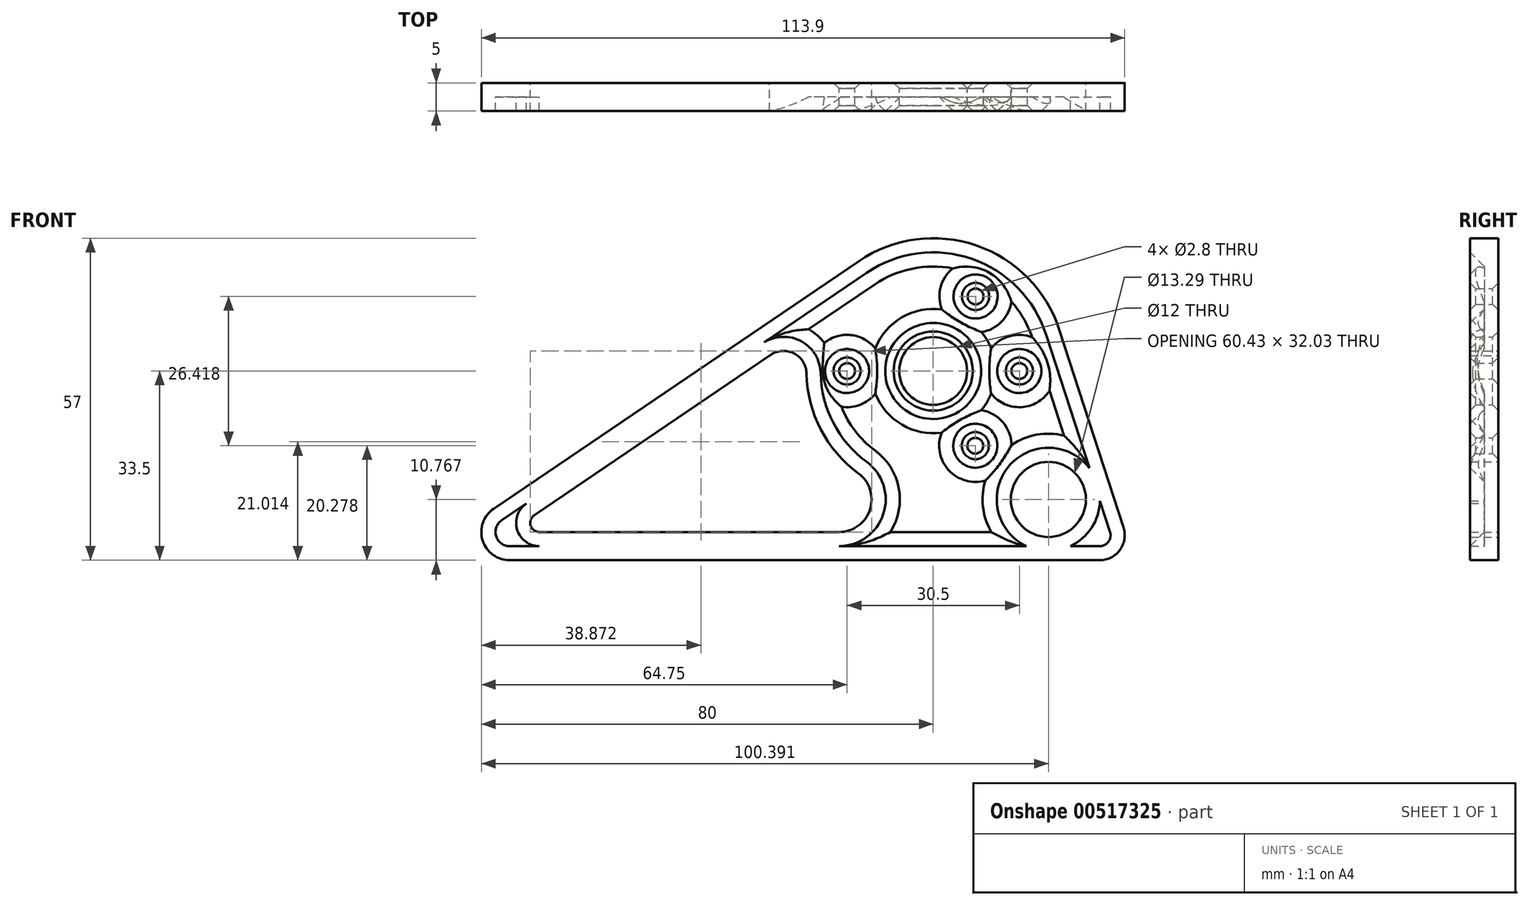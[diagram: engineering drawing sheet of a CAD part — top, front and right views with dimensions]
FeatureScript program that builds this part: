
annotation { "Feature Type Name" : "Feature", "Feature Type Description" : "" }
export const myFeature = defineFeature(function(context is Context, id is Id, definition is map)
    precondition{}
    {
        {
            var Q0;
            Q0=qCreatedBy(makeId("Front.planeOp"),FACE);
            var sketch = newSketch(context, id + "F0", { "sketchPlane" : qUnion([Q0])});
            skCircle(sketch, "E0", {"center": v(0, 0) * mm, "radius": 18.5 * mm});
            skCircle(sketch, "E1", {"center": v(0, 0) * mm, "radius": 6 * mm});
            skArc(sketch, "E2", {"start": v(-1.66, 2.5) * mm, "mid": v(0, -3) * mm, "end": v(1.66, 2.5) * mm});
            skLineSegment(sketch, "E3", {"start": v(-1.66, 2.5) * mm, "end": v(1.66, 2.5) * mm});
            skCircle(sketch, "E4", {"center": v(-15.25, 0) * mm, "radius": 1.4 * mm});
            skCircle(sketch, "E5", {"center": v(15.25, 0) * mm, "radius": 1.4 * mm});
            skCircle(sketch, "E6", {"center": v(7.5, 13.2) * mm, "radius": 1.4 * mm});
            skCircle(sketch, "E7", {"center": v(7.45, -13.22) * mm, "radius": 1.4 * mm});
            skLineSegment(sketch, "E8", {"start": v(-13.2, 0) * mm, "end": v(13.2, 0) * mm, "construction": true});
            skLineSegment(sketch, "E9", {"start": v(0, -13.2) * mm, "end": v(0, 13.2) * mm, "construction": true});
            skLineSegment(sketch, "E10", {"start": v(7.5, -13.2) * mm, "end": v(7.5, 13.2) * mm, "construction": true});
            skLineSegment(sketch, "E11", {"start": v(-75, -33.5) * mm, "end": v(0, -33.5) * mm});
            skArc(sketch, "E12", {"start": v(-75, -33.5) * mm, "mid": v(-78.54, -32.04) * mm, "end": v(-80, -28.5) * mm});
            skLineSegment(sketch, "E13", {"start": v(-15.25, 0) * mm, "end": v(0, 0) * mm, "construction": true});
            skLineSegment(sketch, "E14", {"start": v(7.5, 13.2) * mm, "end": v(0, 0) * mm, "construction": true});
            skLineSegment(sketch, "E15", {"start": v(15.25, 0) * mm, "end": v(0, 0) * mm, "construction": true});
            skLineSegment(sketch, "E16", {"start": v(7.45, -13.22) * mm, "end": v(0, 0) * mm, "construction": true});
            skLineSegment(sketch, "E17", {"start": v(-80, -28.5) * mm, "end": v(-80, 18.5) * mm});
            skCircle(sketch, "E18", {"center": v(0, 0) * mm, "radius": 28.5 * mm});
            skCircle(sketch, "E19", {"center": v(-75, 18.5) * mm, "radius": 10 * mm});
            skPoint(sketch, "E20", {"position": v(-75, 28.5) * mm});
            skPoint(sketch, "E21", {"position": v(0, 28.5) * mm});
            skArc(sketch, "E22", {"start": v(-80, 18.5) * mm, "mid": v(-78.54, 22.04) * mm, "end": v(-75, 23.5) * mm});
            skLineSegment(sketch, "E23", {"start": v(0, 23.5) * mm, "end": v(-75, 23.5) * mm});
            skCircle(sketch, "E24", {"center": v(-75, 18.5) * mm, "radius": 2.5 * mm});
            skArc(sketch, "E25", {"start": v(-70.63, -25.54) * mm, "mid": v(-71.27, -27.36) * mm, "end": v(-69.72, -28.5) * mm});
            skArc(sketch, "E26", {"start": v(-13.27, -18.08) * mm, "mid": v(-19.9, -10.33) * mm, "end": v(-22.42, -0.44) * mm});
            skLineSegment(sketch, "E27", {"start": v(-69.72, -28.5) * mm, "end": v(-16.68, -28.5) * mm});
            skLineSegment(sketch, "E28", {"start": v(0, -33.5) * mm, "end": v(29.47, -33.5) * mm});
            skArc(sketch, "E29", {"start": v(29.47, -33.5) * mm, "mid": v(33.05, -31.68) * mm, "end": v(33.68, -27.7) * mm});
            skLineSegment(sketch, "E30", {"start": v(33.68, -27.7) * mm, "end": v(22.36, 7.25) * mm});
            skArc(sketch, "E31", {"start": v(22.36, 7.25) * mm, "mid": v(13.82, 19) * mm, "end": v(0, 23.5) * mm});
            skCircle(sketch, "E32", {"center": v(20.4, -22.73) * mm, "radius": 6.64 * mm});
            skArc(sketch, "E33", {"start": v(0, 23.5) * mm, "mid": v(-6.9, 22.46) * mm, "end": v(-13.19, 19.45) * mm});
            skLineSegment(sketch, "E34", {"start": v(-13.19, 19.45) * mm, "end": v(-77.8, -24.36) * mm});
            skArc(sketch, "E35", {"start": v(-77.8, -24.36) * mm, "mid": v(-79.78, -29.97) * mm, "end": v(-75, -33.5) * mm});
            skArc(sketch, "E36", {"start": v(-22.42, -0.44) * mm, "mid": v(-24.74, 3.15) * mm, "end": v(-28.98, 2.7) * mm});
            skArc(sketch, "E37", {"start": v(-13.27, -18.08) * mm, "mid": v(-11.2, -24.53) * mm, "end": v(-16.68, -28.5) * mm});
            skLineSegment(sketch, "E38", {"start": v(-70.63, -25.54) * mm, "end": v(-28.98, 2.7) * mm});
            skSolve(sketch);
        }
        {
            var Q0;
            Q0=qCreatedBy(makeId("Front.planeOp"),FACE);
            cPlane(context, id + "F1", {"entities" : qUnion([Q0]), "cplaneType" : CPlaneType.OFFSET, "offset" : 50 * mm, "width" : 150 * mm, "height" : 150 * mm});
        }
        {
            var Q0;
            Q0=makeQuery(id+"F0.imprint","IMPRINT",FACE,{"disambiguationData":[TD([[makeQuery(id+"F0.imprint","IMPRINT",EDGE,{"derivedFrom":sQuery(id+"F0.wireOp",EDGE,"E0")}),1.0]])]});
            var Q1;
            {var subQ4=sQuery(id+"F0.wireOp",EDGE,"E11");Q1=makeQuery(id+"F0.imprint","IMPRINT",FACE,{"disambiguationData":[TD([[makeQuery(id+"F0.imprint","IMPRINT",EDGE,{"derivedFrom":subQ4}),1.0]])]});}
            var Q2;
            Q2=makeQuery(id+"F0.imprint","IMPRINT",FACE,{"disambiguationData":[TD([[makeQuery(id+"F0.imprint","IMPRINT",EDGE,{"derivedFrom":sQuery(id+"F0.wireOp",EDGE,"E0")}),-1.0]])]});
            extrude(context, id + "F2", {"entities" : qUnion([Q0, Q1, Q2]), "endBound" : BoundingType.SYMMETRIC, "depth" : 5 * mm, "offsetDistance" : 25 * mm});
        }
        {
            var Q0;
            Q0=makeQuery(id+"F2.opExtrude","CAP_FACE",FACE,{"disambiguationData":[OSD([sQuery(id+"F0.wireOp",EDGE,"E1"),sQuery(id+"F0.wireOp",EDGE,"E4"),sQuery(id+"F0.wireOp",EDGE,"E5"),sQuery(id+"F0.wireOp",EDGE,"E6"),sQuery(id+"F0.wireOp",EDGE,"E7"),sQuery(id+"F0.wireOp",EDGE,"E11"),sQuery(id+"F0.wireOp",EDGE,"E25"),sQuery(id+"F0.wireOp",EDGE,"E26"),sQuery(id+"F0.wireOp",EDGE,"E27"),sQuery(id+"F0.wireOp",EDGE,"E28"),sQuery(id+"F0.wireOp",EDGE,"E29"),sQuery(id+"F0.wireOp",EDGE,"E30"),sQuery(id+"F0.wireOp",EDGE,"E31"),sQuery(id+"F0.wireOp",EDGE,"E32"),sQuery(id+"F0.wireOp",EDGE,"E33"),sQuery(id+"F0.wireOp",EDGE,"E34"),sQuery(id+"F0.wireOp",EDGE,"E35"),sQuery(id+"F0.wireOp",EDGE,"E36"),sQuery(id+"F0.wireOp",EDGE,"E37"),sQuery(id+"F0.wireOp",EDGE,"E38")])],"isStart":false});
            shell(context, id + "F3", {"entities" : qUnion([Q0]), "thickness" : 2.5 * mm});
        }
        {
            var Q0;
            {var subQ0=sQuery(id+"F0.wireOp",EDGE,"E38");var subQ1=sQuery(id+"F0.wireOp",EDGE,"E37");var subQ2=sQuery(id+"F0.wireOp",EDGE,"E36");var subQ3=sQuery(id+"F0.wireOp",EDGE,"E35");var subQ4=sQuery(id+"F0.wireOp",EDGE,"E34");var subQ5=sQuery(id+"F0.wireOp",EDGE,"E33");var subQ6=sQuery(id+"F0.wireOp",EDGE,"E32");var subQ7=sQuery(id+"F0.wireOp",EDGE,"E31");var subQ8=sQuery(id+"F0.wireOp",EDGE,"E30");var subQ9=sQuery(id+"F0.wireOp",EDGE,"E29");var subQ10=sQuery(id+"F0.wireOp",EDGE,"E28");var subQ11=sQuery(id+"F0.wireOp",EDGE,"E27");var subQ12=sQuery(id+"F0.wireOp",EDGE,"E26");var subQ13=sQuery(id+"F0.wireOp",EDGE,"E25");var subQ14=sQuery(id+"F0.wireOp",EDGE,"E11");var subQ15=sQuery(id+"F0.wireOp",EDGE,"E7");var subQ16=sQuery(id+"F0.wireOp",EDGE,"E6");var subQ17=sQuery(id+"F0.wireOp",EDGE,"E5");var subQ18=sQuery(id+"F0.wireOp",EDGE,"E4");var subQ19=sQuery(id+"F0.wireOp",EDGE,"E1");Q0=makeQuery(id+"F3.opShell","OFFSET_FACE",FACE,{"disambiguationData":[OSD([subQ19,subQ18,subQ17,subQ16,subQ15,subQ14,subQ13,subQ12,subQ11,subQ10,subQ9,subQ8,subQ7,subQ6,subQ5,subQ4,subQ3,subQ2,subQ1,subQ0]),TDD([makeQuery(id+"F2.opExtrude","CAP_FACE",FACE,{"disambiguationData":[OSD([subQ19,subQ18,subQ17,subQ16,subQ15,subQ14,subQ13,subQ12,subQ11,subQ10,subQ9,subQ8,subQ7,subQ6,subQ5,subQ4,subQ3,subQ2,subQ1,subQ0])],"isStart":true})]),OD(2.0)]});}
            chamfer(context, id + "F4", {"entities" : qUnion([Q0]), "width" : 2.5 * mm, "tangentPropagation" : true});
        }
        {
            var Q0;
            Q0=makeQuery(id+"F2.opExtrude","SWEPT_FACE",FACE,{"disambiguationData":[OSD([sQuery(id+"F0.wireOp",EDGE,"E4")])]});
            var Q1;
            Q1=makeQuery(id+"F2.opExtrude","SWEPT_FACE",FACE,{"disambiguationData":[OSD([sQuery(id+"F0.wireOp",EDGE,"E7")])]});
            var Q2;
            Q2=makeQuery(id+"F2.opExtrude","SWEPT_FACE",FACE,{"disambiguationData":[OSD([sQuery(id+"F0.wireOp",EDGE,"E5")])]});
            var Q3;
            Q3=makeQuery(id+"F2.opExtrude","SWEPT_FACE",FACE,{"disambiguationData":[OSD([sQuery(id+"F0.wireOp",EDGE,"E6")])]});
            var Q4;
            Q4=makeQuery(id+"F2.opExtrude","SWEPT_FACE",FACE,{"disambiguationData":[OSD([sQuery(id+"F0.wireOp",EDGE,"E1")])]});
            chamfer(context, id + "F5", {"entities" : qUnion([Q0, Q1, Q2, Q3, Q4]), "width" : 1 * mm, "tangentPropagation" : true});
        }
    });
